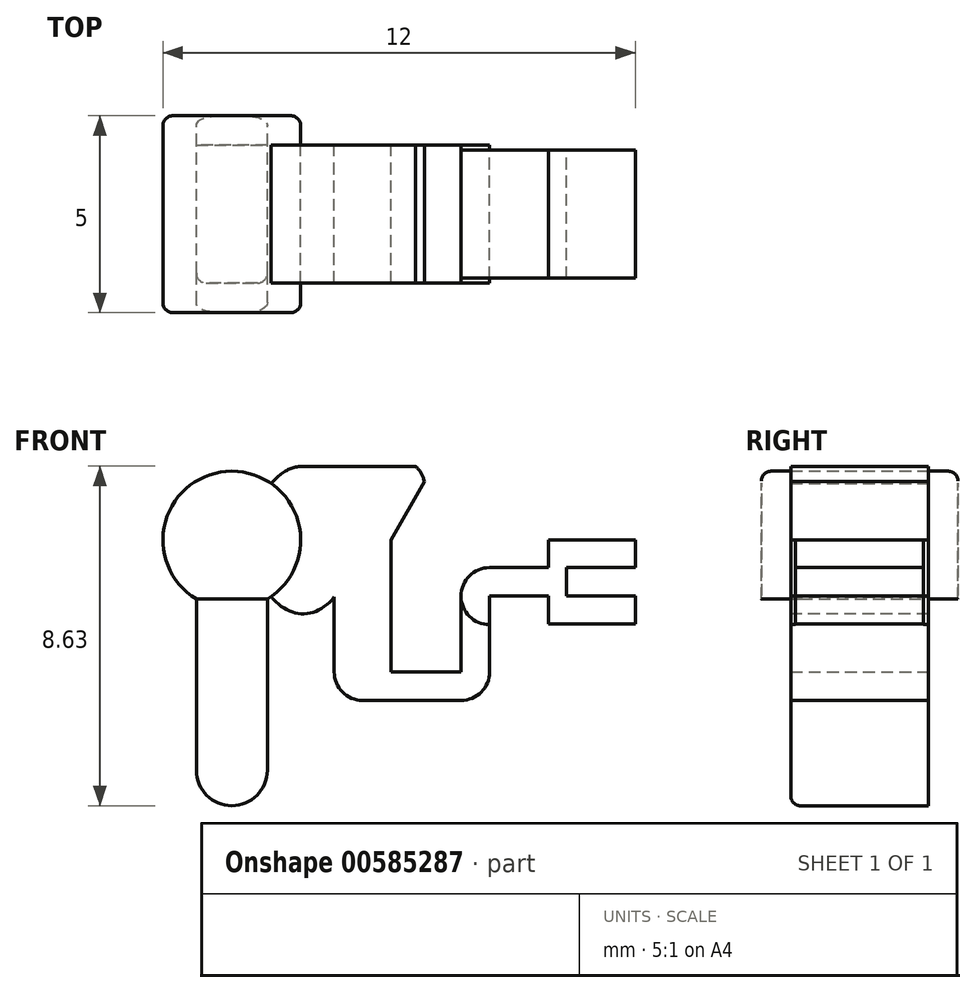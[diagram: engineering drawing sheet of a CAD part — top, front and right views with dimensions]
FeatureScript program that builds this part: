
annotation { "Feature Type Name" : "Feature", "Feature Type Description" : "" }
export const myFeature = defineFeature(function(context is Context, id is Id, definition is map)
    precondition{}
    {
        {
            var Q0;
            Q0=qCreatedBy(makeId("Front.planeOp"),FACE);
            var sketch = newSketch(context, id + "F0", { "sketchPlane" : qUnion([Q0])});
            skArc(sketch, "E0", {"start": v(0.9, -1.5) * mm, "mid": v(0, 1.75) * mm, "end": v(-0.9, -1.5) * mm});
            skLineSegment(sketch, "E1", {"start": v(-0.9, -1.5) * mm, "end": v(-0.9, -5.85) * mm});
            skLineSegment(sketch, "E2", {"start": v(0.9, -5.85) * mm, "end": v(0.9, -1.5) * mm});
            skPoint(sketch, "E3", {"position": v(0, 1.75) * mm});
            skArc(sketch, "E4", {"start": v(-0.9, -5.85) * mm, "mid": v(0, -6.75) * mm, "end": v(0.9, -5.85) * mm});
            skLineSegment(sketch, "E5", {"start": v(0.9, -1.5) * mm, "end": v(-0.9, -1.5) * mm});
            skSolve(sketch);
        }
        {
            var Q0;
            Q0=makeQuery(id+"F0.imprint","IMPRINT",FACE,{"disambiguationData":[TD([[makeQuery(id+"F0.imprint","IMPRINT",EDGE,{"derivedFrom":sQuery(id+"F0.wireOp",EDGE,"E0")}),1.0]])]});
            extrude(context, id + "F1", {"entities" : qUnion([Q0]), "endBound" : BoundingType.SYMMETRIC, "depth" : 5 * mm, "offsetDistance" : 25 * mm});
        }
        {
            var Q0;
            Q0=makeQuery(id+"F0.imprint","IMPRINT",FACE,{"disambiguationData":[TD([[makeQuery(id+"F0.imprint","IMPRINT",EDGE,{"derivedFrom":sQuery(id+"F0.wireOp",EDGE,"E1")}),1.0]])]});
            extrude(context, id + "F2", {"entities" : qUnion([Q0]), "operationType" : NewBodyOperationType.ADD, "endBound" : BoundingType.SYMMETRIC, "depth" : 3.5 * mm, "offsetDistance" : 25 * mm});
        }
        {
            var Q0;
            Q0=makeQuery(id+"F2.opExtrude","CAP_EDGE",EDGE,{"disambiguationData":[OSD([sQuery(id+"F0.wireOp",EDGE,"E1")])],"isStart":false});
            var Q1;
            Q1=makeQuery(id+"F1.opExtrude","CAP_EDGE",EDGE,{"disambiguationData":[OSD([sQuery(id+"F0.wireOp",EDGE,"E0")])],"isStart":false});
            var Q2;
            Q2=makeQuery(id+"F1.opExtrude","CAP_EDGE",EDGE,{"disambiguationData":[OSD([sQuery(id+"F0.wireOp",EDGE,"E0")])],"isStart":true});
            fillet(context, id + "F3", {"entities" : qUnion([Q0, Q1, Q2]), "radius" : 0.25 * mm, "tangentPropagation" : true, "allowEdgeOverflow" : false});
        }
        {
            var Q0;
            Q0=qCreatedBy(makeId("Top.planeOp"),FACE);
            var sketch = newSketch(context, id + "F4", { "sketchPlane" : qUnion([Q0])});
            skArc(sketch, "E6", {"start": v(-2.5, 0) * mm, "mid": v(0, -2.5) * mm, "end": v(2.5, 0) * mm});
            skLineSegment(sketch, "E7", {"start": v(0, 2.5) * mm, "end": v(0, -2.5) * mm, "construction": true});
            skLineSegment(sketch, "E8", {"start": v(-2.5, 0) * mm, "end": v(2.5, 0) * mm});
            skSolve(sketch);
        }
        {
            var Q0;
            Q0=qCreatedBy(makeId("Front.planeOp"),FACE);
            var sketch = newSketch(context, id + "F5", { "sketchPlane" : qUnion([Q0])});
            skPoint(sketch, "E9", {"position": v(1.8, 0) * mm});
            skEllipticalArc(sketch, "E10", {});
            skPoint(sketch, "E11", {"position": v(1, 1.43) * mm});
            skPoint(sketch, "E12", {"position": v(1, -1.43) * mm});
            skArc(sketch, "E13", {"start": v(1, -1.43) * mm, "mid": v(1.75, 0) * mm, "end": v(1, 1.43) * mm});
            skLineSegment(sketch, "E14", {"start": v(1.8, 1.88) * mm, "end": v(4.67, 1.88) * mm});
            skLineSegment(sketch, "E15", {"start": v(4.89, 1.5) * mm, "end": v(4.05, 0) * mm});
            skLineSegment(sketch, "E16", {"start": v(4.05, 0) * mm, "end": v(4.05, -3.35) * mm});
            skLineSegment(sketch, "E17", {"start": v(4.05, -3.35) * mm, "end": v(2.6, -3.35) * mm});
            skLineSegment(sketch, "E18", {"start": v(2.6, -3.35) * mm, "end": v(2.6, -1.45) * mm});
            skArc(sketch, "E19", {"start": v(4.89, 1.5) * mm, "mid": v(4.81, 1.7) * mm, "end": v(4.67, 1.88) * mm});
            skPoint(sketch, "E20", {"position": v(1.8, -1.88) * mm});
            skArc(sketch, "E21", {"start": v(2.6, -3.35) * mm, "mid": v(3.33, -4.07) * mm, "end": v(4.05, -3.35) * mm});
            skPoint(sketch, "E22", {"position": v(4.89, 1.5) * mm});
            skPoint(sketch, "E23", {"position": v(4.67, 1.88) * mm});
            skArc(sketch, "E24.trimOffspring", {"start": v(3.83, 1.88) * mm, "mid": v(3.69, 1.05) * mm, "end": v(4.48, 0.77) * mm});
            skLineSegment(sketch, "E25", {"start": v(4.05, -3.35) * mm, "end": v(5.83, -3.35) * mm});
            skLineSegment(sketch, "E26", {"start": v(6.55, -2.6) * mm, "end": v(6.55, -1.42) * mm});
            skLineSegment(sketch, "E27", {"start": v(5.83, -3.35) * mm, "end": v(5.83, -1.42) * mm});
            skLineSegment(sketch, "E28", {"start": v(6.55, -0.7) * mm, "end": v(8.05, -0.7) * mm});
            skLineSegment(sketch, "E29", {"start": v(8.05, -0.7) * mm, "end": v(8.05, -1.42) * mm});
            skLineSegment(sketch, "E30", {"start": v(8.05, -1.42) * mm, "end": v(6.55, -1.42) * mm});
            skLineSegment(sketch, "E31", {"start": v(3.33, -4.08) * mm, "end": v(5.1, -4.08) * mm});
            skArc(sketch, "E32", {"start": v(6.55, -0.7) * mm, "mid": v(5.83, -1.42) * mm, "end": v(6.55, -2.15) * mm});
            skPoint(sketch, "E33", {"position": v(6.55, -0.7) * mm});
            skPoint(sketch, "E34", {"position": v(5.83, -1.42) * mm});
            skPoint(sketch, "E35", {"position": v(5.1, -3.35) * mm});
            skPoint(sketch, "E36", {"position": v(5.83, -2.6) * mm});
            skLineSegment(sketch, "E37", {"start": v(8.05, -0.7) * mm, "end": v(8.05, 0) * mm});
            skLineSegment(sketch, "E38", {"start": v(8.05, 0) * mm, "end": v(10.25, 0) * mm});
            skLineSegment(sketch, "E39", {"start": v(10.25, 0) * mm, "end": v(10.25, -0.7) * mm});
            skLineSegment(sketch, "E40", {"start": v(10.25, -0.7) * mm, "end": v(8.5, -0.7) * mm});
            skLineSegment(sketch, "E41", {"start": v(8.5, -0.7) * mm, "end": v(8.5, -1.43) * mm});
            skLineSegment(sketch, "E42", {"start": v(8.5, -1.43) * mm, "end": v(10.25, -1.43) * mm});
            skLineSegment(sketch, "E43", {"start": v(10.25, -1.43) * mm, "end": v(10.25, -2.12) * mm});
            skLineSegment(sketch, "E44", {"start": v(10.25, -2.12) * mm, "end": v(8.05, -2.12) * mm});
            skLineSegment(sketch, "E45", {"start": v(8.05, -2.12) * mm, "end": v(8.05, -1.42) * mm});
            skLineSegment(sketch, "E46", {"start": v(9.65, 0) * mm, "end": v(9.65, -0.7) * mm});
            skLineSegment(sketch, "E47", {"start": v(9.65, -1.41) * mm, "end": v(9.65, -2.12) * mm});
            skPoint(sketch, "E48", {"position": v(9.65, -1.41) * mm});
            skPoint(sketch, "E49", {"position": v(9.65, -0.35) * mm});
            skPoint(sketch, "E50", {"position": v(9.65, -1.77) * mm});
            skPoint(sketch, "E51", {"position": v(10.25, -0.35) * mm});
            skLineSegment(sketch, "E52", {"start": v(6.55, -2.6) * mm, "end": v(6.55, -3.35) * mm});
            skArc(sketch, "E53", {"start": v(5.83, -4.08) * mm, "mid": v(6.55, -3.35) * mm, "end": v(5.83, -2.62) * mm});
            skLineSegment(sketch, "E54", {"start": v(5.83, -3.35) * mm, "end": v(5.83, -4.08) * mm});
            skLineSegment(sketch, "E55", {"start": v(5.83, -4.08) * mm, "end": v(5.1, -4.08) * mm});
            skLineSegment(sketch, "E56", {"start": v(5.1, -3.35) * mm, "end": v(5.1, -4.08) * mm});
            skLineSegment(sketch, "E57", {"start": v(5.83, -2.6) * mm, "end": v(6.55, -2.6) * mm});
            skLineSegment(sketch, "E58", {"start": v(6.55, -0.7) * mm, "end": v(6.55, -1.42) * mm});
            const initialGuessF5  = {"E10": [0.0018075004407379397, 0, 0, -1, 0.001875, 0.00125, 5.583455789331897, 3.841322171437482]};
            skSetInitialGuess(sketch, initialGuessF5);
            skSolve(sketch);
        }
        {
            var Q0;
            {var subQ3=sQuery(id+"F5.wireOp",EDGE,"E13");Q0=makeQuery(id+"F5.imprint","IMPRINT",FACE,{"disambiguationData":[TD([[makeQuery(id+"F5.imprint","IMPRINT",EDGE,{"derivedFrom":subQ3}),-1.0]])]});}
            extrude(context, id + "F6", {"entities" : qUnion([Q0]), "endBound" : BoundingType.SYMMETRIC, "depth" : 3.5 * mm, "offsetDistance" : 25 * mm});
        }
        {
            var Q0;
            {var subQ0=sQuery(id+"F5.wireOp",EDGE,"E16");Q0=makeQuery(id+"F5.imprint","IMPRINT",FACE,{"disambiguationData":[TD([[makeQuery(id+"F5.imprint","IMPRINT",EDGE,{"derivedFrom":subQ0}),-1.0]])]});}
            var Q1;
            {var subQ0=sQuery(id+"F5.wireOp",EDGE,"E19");Q1=makeQuery(id+"F5.imprint","IMPRINT",FACE,{"disambiguationData":[TD([[makeQuery(id+"F5.imprint","IMPRINT",EDGE,{"derivedFrom":subQ0}),1.0]])]});}
            extrude(context, id + "F7", {"entities" : qUnion([Q0, Q1]), "operationType" : NewBodyOperationType.ADD, "endBound" : BoundingType.SYMMETRIC, "depth" : 3.5 * mm, "offsetDistance" : 25 * mm});
        }
        {
            var Q0;
            {var subQ0=sQuery(id+"F5.wireOp",EDGE,"E17");Q0=makeQuery(id+"F5.imprint","IMPRINT",FACE,{"disambiguationData":[TD([[makeQuery(id+"F5.imprint","IMPRINT",EDGE,{"derivedFrom":subQ0}),1.0]])]});}
            var Q1;
            {var subQ3=sQuery(id+"F5.wireOp",EDGE,"E31");Q1=makeQuery(id+"F5.imprint","IMPRINT",FACE,{"disambiguationData":[TD([[makeQuery(id+"F5.imprint","IMPRINT",EDGE,{"derivedFrom":subQ3}),1.0]])]});}
            var Q2;
            {var subQ0=sQuery(id+"F5.wireOp",EDGE,"E54");Q2=makeQuery(id+"F5.imprint","IMPRINT",FACE,{"disambiguationData":[TD([[makeQuery(id+"F5.imprint","IMPRINT",EDGE,{"derivedFrom":subQ0}),-1.0]])]});}
            var Q3;
            {var subQ0=sQuery(id+"F5.wireOp",EDGE,"E54");Q3=makeQuery(id+"F5.imprint","IMPRINT",FACE,{"disambiguationData":[TD([[makeQuery(id+"F5.imprint","IMPRINT",EDGE,{"derivedFrom":subQ0}),1.0]])]});}
            var Q4;
            {var subQ4=sQuery(id+"F5.wireOp",EDGE,"E52");Q4=makeQuery(id+"F5.imprint","IMPRINT",FACE,{"disambiguationData":[TD([[makeQuery(id+"F5.imprint","IMPRINT",EDGE,{"derivedFrom":subQ4}),-1.0]])]});}
            var Q5;
            {var subQ0=sQuery(id+"F5.wireOp",EDGE,"E57");Q5=makeQuery(id+"F5.imprint","IMPRINT",FACE,{"disambiguationData":[TD([[makeQuery(id+"F5.imprint","IMPRINT",EDGE,{"derivedFrom":subQ0}),1.0]])]});}
            extrude(context, id + "F8", {"entities" : qUnion([Q0, Q1, Q2, Q3, Q4, Q5]), "operationType" : NewBodyOperationType.ADD, "endBound" : BoundingType.SYMMETRIC, "depth" : 3.5 * mm, "offsetDistance" : 25 * mm});
        }
        {
            var Q0;
            {var subQ0=sQuery(id+"F5.wireOp",EDGE,"E58");Q0=makeQuery(id+"F5.imprint","IMPRINT",FACE,{"disambiguationData":[TD([[makeQuery(id+"F5.imprint","IMPRINT",EDGE,{"derivedFrom":subQ0}),-1.0]])]});}
            var Q1;
            Q1=makeQuery(id+"F5.imprint","IMPRINT",FACE,{"disambiguationData":[TD([[makeQuery(id+"F5.imprint","IMPRINT",EDGE,{"derivedFrom":sQuery(id+"F5.wireOp",EDGE,"E28")}),-1.0]])]});
            var Q2;
            Q2=makeQuery(id+"F5.imprint","IMPRINT",FACE,{"disambiguationData":[TD([[makeQuery(id+"F5.imprint","IMPRINT",EDGE,{"derivedFrom":sQuery(id+"F5.wireOp",EDGE,"E29")}),1.0]])]});
            var Q3;
            {var subQ0=sQuery(id+"F5.wireOp",EDGE,"E39");Q3=makeQuery(id+"F5.imprint","IMPRINT",FACE,{"disambiguationData":[TD([[makeQuery(id+"F5.imprint","IMPRINT",EDGE,{"derivedFrom":subQ0}),-1.0]])]});}
            var Q4;
            {var subQ0=sQuery(id+"F5.wireOp",EDGE,"E43");Q4=makeQuery(id+"F5.imprint","IMPRINT",FACE,{"disambiguationData":[TD([[makeQuery(id+"F5.imprint","IMPRINT",EDGE,{"derivedFrom":subQ0}),-1.0]])]});}
            extrude(context, id + "F9", {"entities" : qUnion([Q0, Q1, Q2, Q3, Q4]), "operationType" : NewBodyOperationType.ADD, "endBound" : BoundingType.SYMMETRIC, "depth" : 3.25 * mm, "offsetDistance" : 25 * mm});
        }
    });
